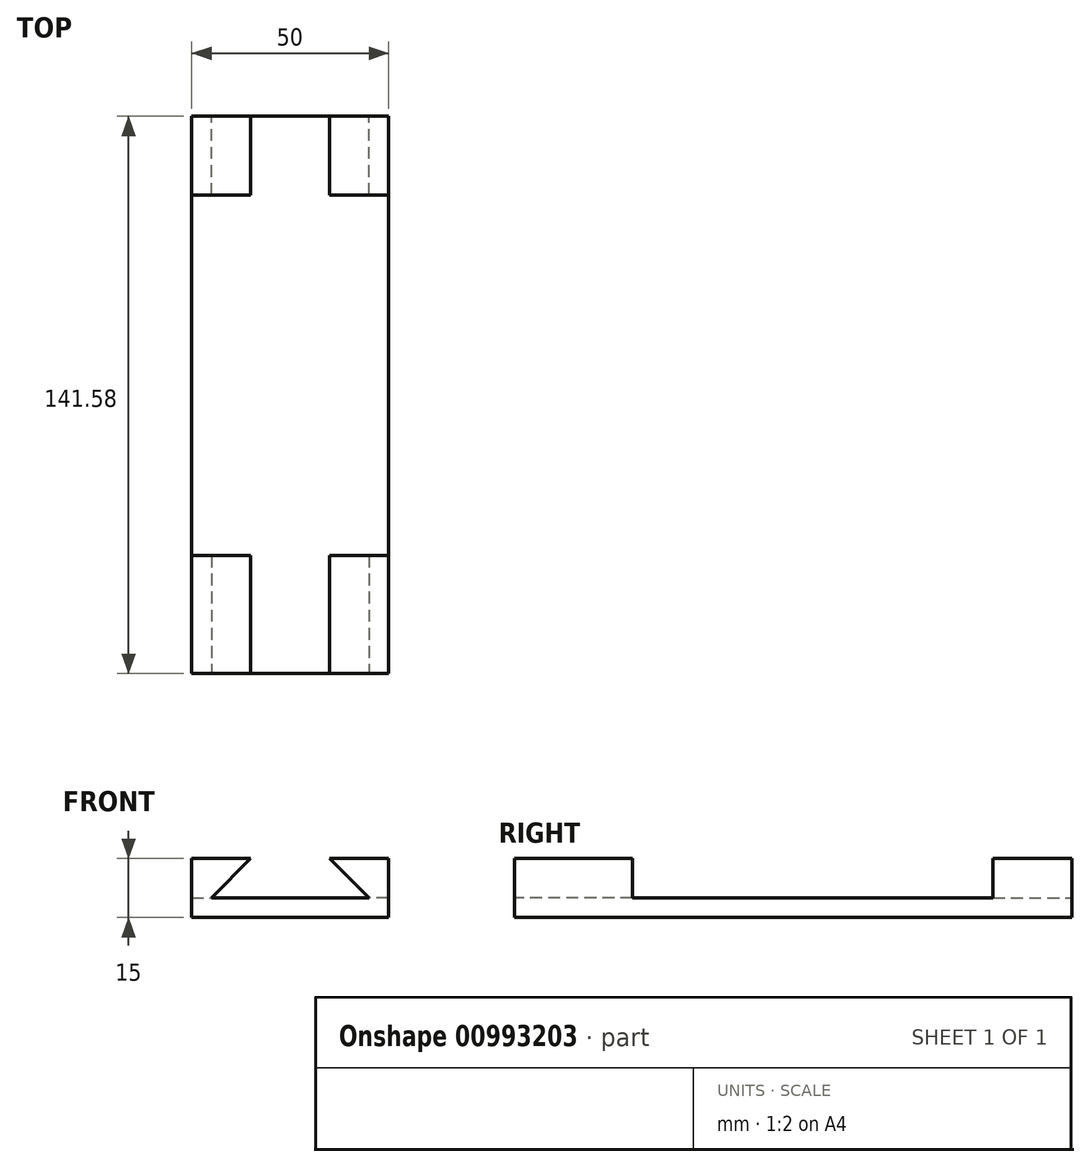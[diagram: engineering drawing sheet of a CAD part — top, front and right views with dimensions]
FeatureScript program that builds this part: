
annotation { "Feature Type Name" : "Feature", "Feature Type Description" : "" }
export const myFeature = defineFeature(function(context is Context, id is Id, definition is map)
    precondition{}
    {
        {
            var Q0;
            Q0=qCreatedBy(makeId("Top.planeOp"),FACE);
            var sketch = newSketch(context, id + "F0", { "sketchPlane" : qUnion([Q0])});
            skLineSegment(sketch, "E0.bottom", {"start": v(-25, 70.8) * mm, "end": v(25, 70.8) * mm});
            skLineSegment(sketch, "E0.top", {"start": v(-25, -70.8) * mm, "end": v(25, -70.8) * mm});
            skLineSegment(sketch, "E0.left", {"start": v(-25, 70.8) * mm, "end": v(-25, -70.8) * mm});
            skLineSegment(sketch, "E0.right", {"start": v(25, 70.8) * mm, "end": v(25, -70.8) * mm});
            skPoint(sketch, "E0.middle", {"position": v(0, 0) * mm});
            skSolve(sketch);
        }
        {
            var Q0;
            Q0 = qSketchRegion(id + "F0", true);
            extrude(context, id + "F1", {"entities" : qUnion([Q0]), "oppositeDirection" : true, "depth" : 5 * mm, "offsetDistance" : 25 * mm});
        }
        {
            var Q0;
            Q0=qCreatedBy(makeId("Front.planeOp"),FACE);
            cPlane(context, id + "F2", {"entities" : qUnion([Q0]), "cplaneType" : CPlaneType.OFFSET, "offset" : 70.8 * mm, "width" : 150 * mm, "height" : 150 * mm});
        }
        {
            var Q0;
            Q0=qCreatedBy(id+"F2.planeOp",FACE);
            var sketch = newSketch(context, id + "F3", { "sketchPlane" : qUnion([Q0])});
            skLineSegment(sketch, "E1", {"start": v(-25, 0) * mm, "end": v(-25, 10) * mm});
            skLineSegment(sketch, "E2", {"start": v(-25, 10) * mm, "end": v(-10, 10) * mm});
            skLineSegment(sketch, "E3", {"start": v(-10, 10) * mm, "end": v(-20, 0) * mm});
            skLineSegment(sketch, "E4", {"start": v(-20, 0) * mm, "end": v(20, 0) * mm});
            skLineSegment(sketch, "E5", {"start": v(20, 0) * mm, "end": v(10, 10) * mm});
            skLineSegment(sketch, "E6", {"start": v(10, 10) * mm, "end": v(25, 10) * mm});
            skLineSegment(sketch, "E7", {"start": v(25, 10) * mm, "end": v(25, 0) * mm});
            skLineSegment(sketch, "E8", {"start": v(25, 0) * mm, "end": v(-25, 0) * mm});
            skSolve(sketch);
        }
        {
            var Q0;
            Q0 = qSketchRegion(id + "F3", true);
            extrude(context, id + "F4", {"entities" : qUnion([Q0]), "operationType" : NewBodyOperationType.ADD, "oppositeDirection" : true, "depth" : 30 * mm, "offsetDistance" : 25 * mm});
        }
        {
            var Q0;
            Q0=qCreatedBy(makeId("Front.planeOp"),FACE);
            cPlane(context, id + "F5", {"entities" : qUnion([Q0]), "cplaneType" : CPlaneType.OFFSET, "offset" : 70.8 * mm, "oppositeDirection" : true, "width" : 150 * mm, "height" : 150 * mm});
        }
        {
            var Q0;
            Q0=qCreatedBy(id+"F5.planeOp",FACE);
            var sketch = newSketch(context, id + "F6", { "sketchPlane" : qUnion([Q0])});
            skLineSegment(sketch, "E9", {"start": v(25, 0) * mm, "end": v(25, 10) * mm});
            skLineSegment(sketch, "E10", {"start": v(25, 10) * mm, "end": v(10, 10) * mm});
            skLineSegment(sketch, "E11", {"start": v(10, 10) * mm, "end": v(20, 0) * mm});
            skLineSegment(sketch, "E12", {"start": v(20, 0) * mm, "end": v(-20, 0) * mm});
            skLineSegment(sketch, "E13", {"start": v(-20, 0) * mm, "end": v(-10, 10) * mm});
            skLineSegment(sketch, "E14", {"start": v(-10, 10) * mm, "end": v(-25, 10) * mm});
            skLineSegment(sketch, "E15", {"start": v(-25, 10) * mm, "end": v(-25, 0) * mm});
            skLineSegment(sketch, "E16", {"start": v(-25, 0) * mm, "end": v(25, 0) * mm});
            skSolve(sketch);
        }
        {
            var Q0;
            Q0 = qSketchRegion(id + "F6", true);
            extrude(context, id + "F7", {"entities" : qUnion([Q0]), "operationType" : NewBodyOperationType.ADD, "depth" : 20 * mm, "offsetDistance" : 25 * mm});
        }
    });
